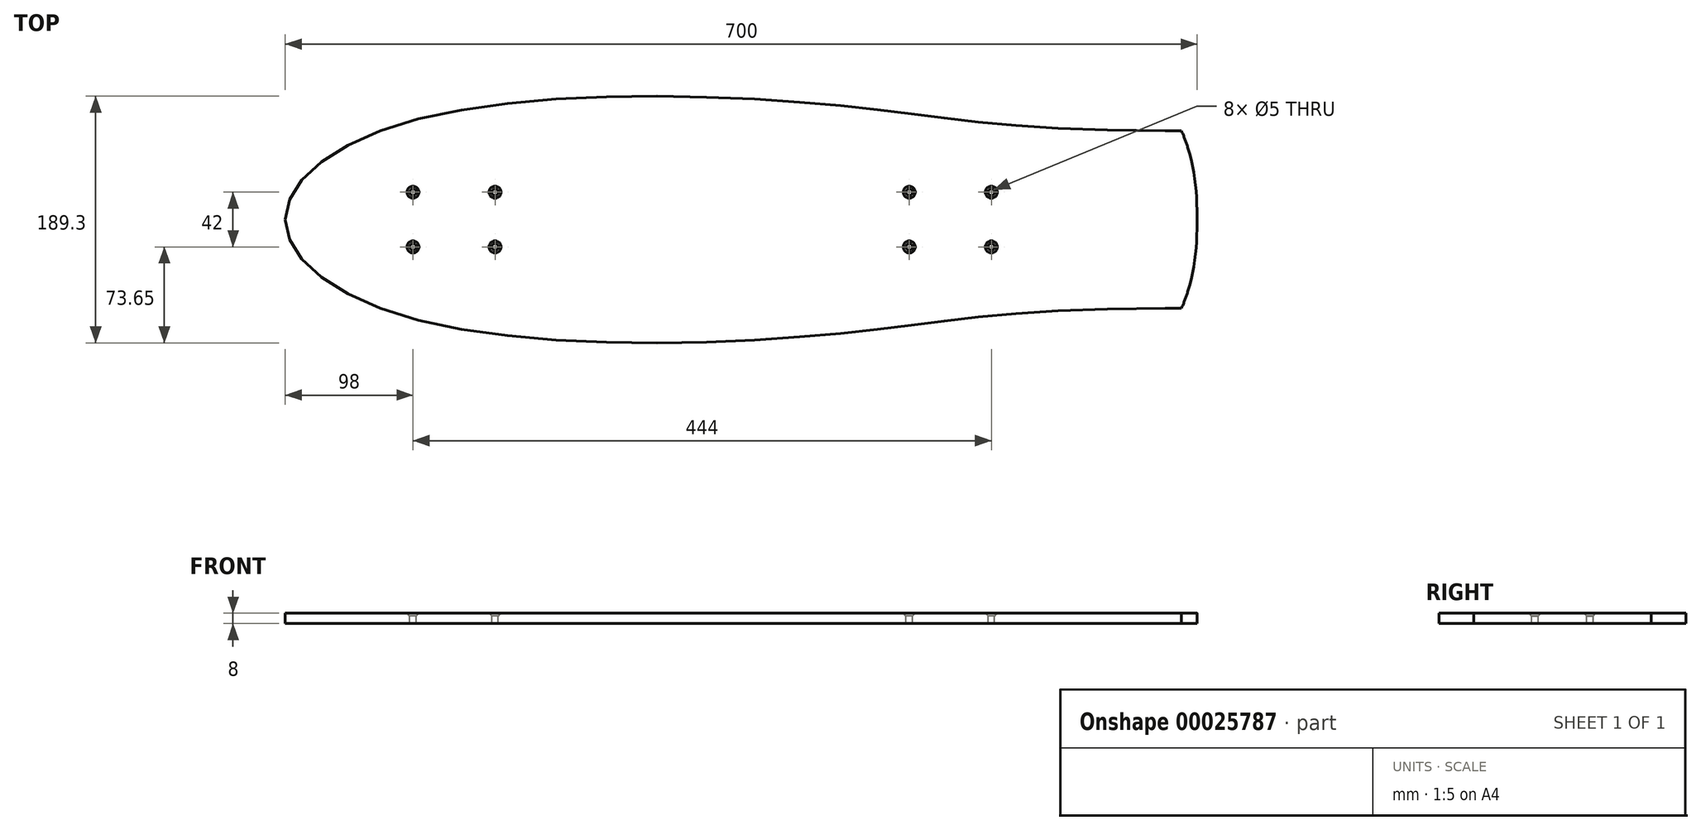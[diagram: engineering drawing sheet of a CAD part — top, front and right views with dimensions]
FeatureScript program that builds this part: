
annotation { "Feature Type Name" : "Feature", "Feature Type Description" : "" }
export const myFeature = defineFeature(function(context is Context, id is Id, definition is map)
    precondition{}
    {
        {
            var Q0;
            Q0=qCreatedBy(makeId("Top.planeOp"),FACE);
            var sketch = newSketch(context, id + "F0", { "sketchPlane" : qUnion([Q0])});
            skLineSegment(sketch, "E0.bottom", {"start": v(-320, 95) * mm, "end": v(380, 95) * mm, "construction": true});
            skLineSegment(sketch, "E0.top", {"start": v(-320, -95) * mm, "end": v(380, -95) * mm, "construction": true});
            skLineSegment(sketch, "E0.left", {"start": v(-320, 95) * mm, "end": v(-320, -95) * mm, "construction": true});
            skLineSegment(sketch, "E1", {"start": v(-200, 95) * mm, "end": v(-200, -95) * mm, "construction": true});
            skLineSegment(sketch, "E2.0", {"start": v(200, 95) * mm, "end": v(200, -95) * mm, "construction": true});
            skLineSegment(sketch, "E3", {"start": v(-200, 0) * mm, "end": v(200, 0) * mm, "construction": true});
            skLineSegment(sketch, "E4.0", {"start": v(-222, 95) * mm, "end": v(-222, -95) * mm, "construction": true});
            skLineSegment(sketch, "E5.0", {"start": v(-159, 95) * mm, "end": v(-159, -95) * mm, "construction": true});
            skLineSegment(sketch, "E6", {"start": v(0, -95) * mm, "end": v(0, 95) * mm, "construction": true});
            skCircle(sketch, "E7", {"center": v(-159, 21) * mm, "radius": 2.5 * mm});
            skCircle(sketch, "E8", {"center": v(-222, 21) * mm, "radius": 2.5 * mm});
            skCircle(sketch, "E9.MirrorC", {"center": v(-222, -21) * mm, "radius": 2.5 * mm});
            skCircle(sketch, "E10.MirrorC", {"center": v(-159, -21) * mm, "radius": 2.5 * mm});
            skCircle(sketch, "E11.MirrorC", {"center": v(222, -21) * mm, "radius": 2.5 * mm});
            skCircle(sketch, "E12.MirrorC", {"center": v(222, 21) * mm, "radius": 2.5 * mm});
            skCircle(sketch, "E13.MirrorC", {"center": v(159, 21) * mm, "radius": 2.5 * mm});
            skCircle(sketch, "E14.MirrorC", {"center": v(159, -21) * mm, "radius": 2.5 * mm});
            skLineSegment(sketch, "E15.0", {"start": v(519.4, 68) * mm, "end": v(305, 68) * mm, "construction": true});
            skLineSegment(sketch, "E16.0", {"start": v(529.49, -68.17) * mm, "end": v(305, -68) * mm, "construction": true});
            skPoint(sketch, "E17.visualSharp", {"position": v(519.4, 68) * mm});
            skPoint(sketch, "E18.visualSharp", {"position": v(529.49, -68.17) * mm});
            skLineSegment(sketch, "E19", {"start": v(380, 95) * mm, "end": v(380, -95) * mm, "construction": true});
            skFitSpline(sketch, "E20", {"points": [v(-320, 0) * mm, v(-235.18, -72.24) * mm, v(102.04, -87.8) * mm, v(368, -68.05) * mm], "startDerivative": vector(0, -358.64) * mm, "endDerivative": vector(1176.2, -2.69) * mm});
            skFitSpline(sketch, "E21.MirrorCS", {"points": [v(-320, 0) * mm, v(-235.18, 72.24) * mm, v(102.04, 87.8) * mm, v(368, 68.05) * mm], "startDerivative": vector(0, 358.64) * mm, "endDerivative": vector(1176.2, 2.69) * mm});
            skFitSpline(sketch, "E22", {"points": [v(368, 68.05) * mm, v(380, 0) * mm, v(368, -68.05) * mm], "startDerivative": vector(60, -136) * mm, "endDerivative": vector(-60, -136) * mm});
            skArc(sketch, "E23.filletArc", {"start": v(372.74, 55.54) * mm, "mid": v(366.23, 64.58) * mm, "end": v(355.65, 68.05) * mm});
            skArc(sketch, "E24.filletArc", {"start": v(355.65, -68.05) * mm, "mid": v(366.23, -64.58) * mm, "end": v(372.74, -55.54) * mm});
            skSolve(sketch);
        }
        {
            var Q0;
            Q0 = qSketchRegion(id + "F0", true);
            extrude(context, id + "F1", {"entities" : qUnion([Q0]), "oppositeDirection" : true, "depth" : 8 * mm});
        }
        {
            var Q0;
            Q0=makeQuery(id+"F1.opExtrude","CAP_EDGE",EDGE,{"disambiguationData":[OSD([sQuery(id+"F0.wireOp",EDGE,"E8")])],"isStart":true});
            var Q1;
            Q1=makeQuery(id+"F1.opExtrude","CAP_EDGE",EDGE,{"disambiguationData":[OSD([sQuery(id+"F0.wireOp",EDGE,"E7")])],"isStart":true});
            var Q2;
            Q2=makeQuery(id+"F1.opExtrude","CAP_EDGE",EDGE,{"disambiguationData":[OSD([sQuery(id+"F0.wireOp",EDGE,"E10.MirrorC")])],"isStart":true});
            var Q3;
            Q3=makeQuery(id+"F1.opExtrude","CAP_EDGE",EDGE,{"disambiguationData":[OSD([sQuery(id+"F0.wireOp",EDGE,"E9.MirrorC")])],"isStart":true});
            var Q4;
            Q4=makeQuery(id+"F1.opExtrude","CAP_EDGE",EDGE,{"disambiguationData":[OSD([sQuery(id+"F0.wireOp",EDGE,"E12.MirrorC")])],"isStart":true});
            var Q5;
            Q5=makeQuery(id+"F1.opExtrude","CAP_EDGE",EDGE,{"disambiguationData":[OSD([sQuery(id+"F0.wireOp",EDGE,"E13.MirrorC")])],"isStart":true});
            var Q6;
            Q6=makeQuery(id+"F1.opExtrude","CAP_EDGE",EDGE,{"disambiguationData":[OSD([sQuery(id+"F0.wireOp",EDGE,"E14.MirrorC")])],"isStart":true});
            var Q7;
            Q7=makeQuery(id+"F1.opExtrude","CAP_EDGE",EDGE,{"disambiguationData":[OSD([sQuery(id+"F0.wireOp",EDGE,"E11.MirrorC")])],"isStart":true});
            chamfer(context, id + "F2", {"entities" : qUnion([Q0, Q1, Q2, Q3, Q4, Q5, Q6, Q7]), "width" : 2.1 * mm, "tangentPropagation" : true});
        }
    });
